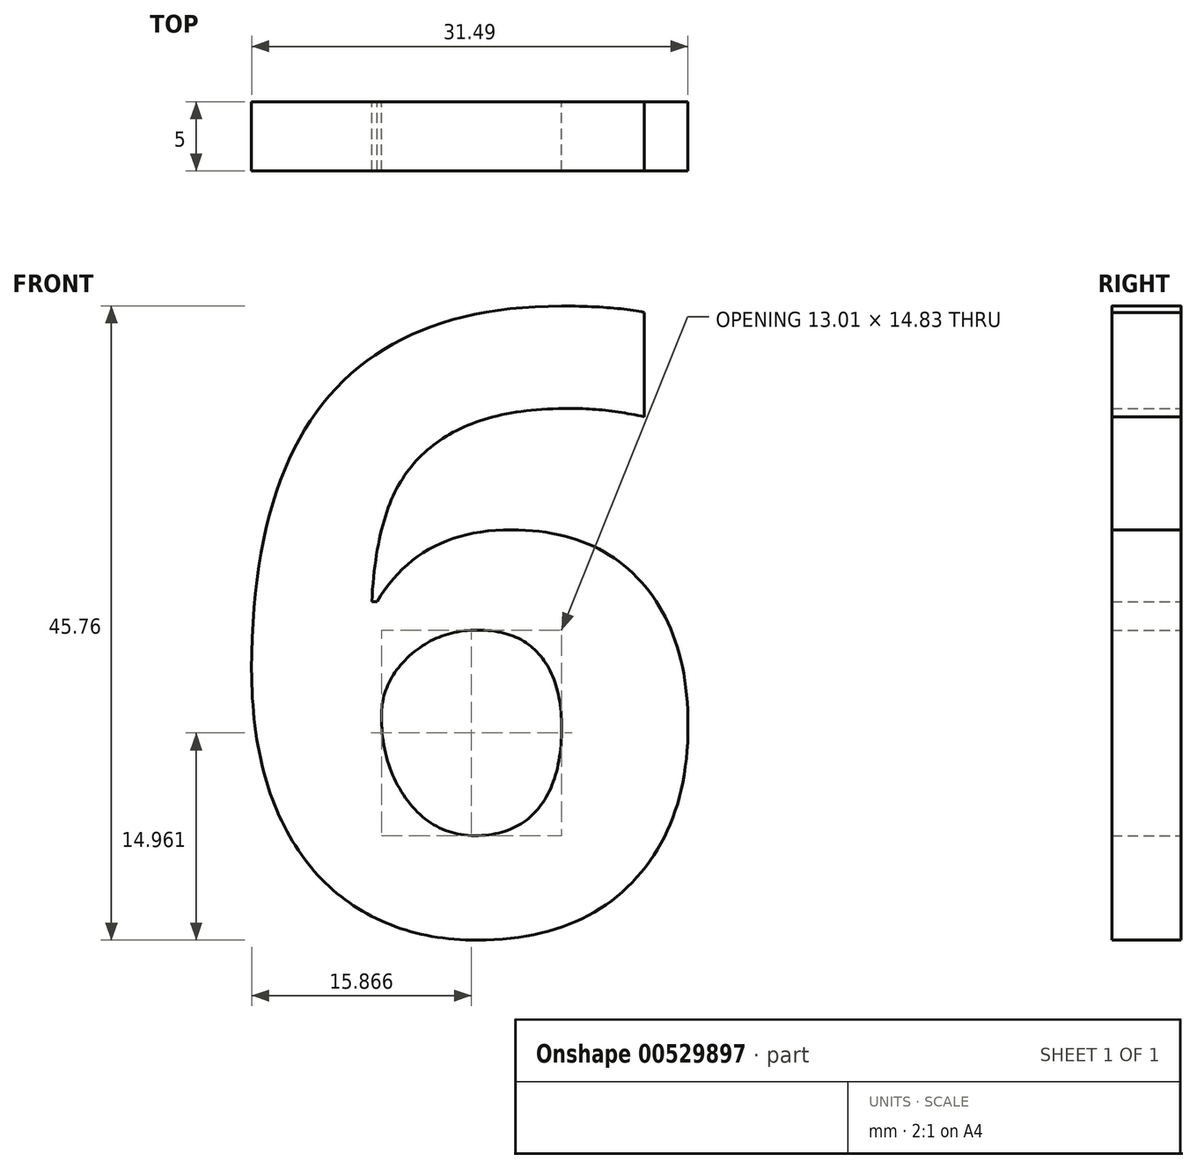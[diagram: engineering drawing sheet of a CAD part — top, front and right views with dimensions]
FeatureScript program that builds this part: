
annotation { "Feature Type Name" : "Feature", "Feature Type Description" : "" }
export const myFeature = defineFeature(function(context is Context, id is Id, definition is map)
    precondition{}
    {
        {
            var Q0;
            Q0=qCreatedBy(makeId("Front.planeOp"),FACE);
            var sketch = newSketch(context, id + "F0", { "sketchPlane" : qUnion([Q0])});
            skText(sketch, "E0", { "text": "6", "fontName": "OpenSans-Bold.ttf"});
            const initialGuessF0  = {"E0": [-0.06496, 0.02158, 1, 0, 0.045]};
            skSetInitialGuess(sketch, initialGuessF0);
            skSolve(sketch);
        }
        {
            var Q0;
            Q0=makeQuery(id+"F0.imprint","IMPRINT",FACE,{"disambiguationData":[TD([[makeQuery(id+"F0.imprint","IMPRINT",EDGE,{"derivedFrom":sQuery(id+"F0.wireOp",EDGE,"E0.sketch_text.stroke-0")}),-1.0]])]});
            extrude(context, id + "F1", {"entities" : qUnion([Q0]), "depth" : 5 * mm, "offsetDistance" : 25 * mm});
        }
    });
